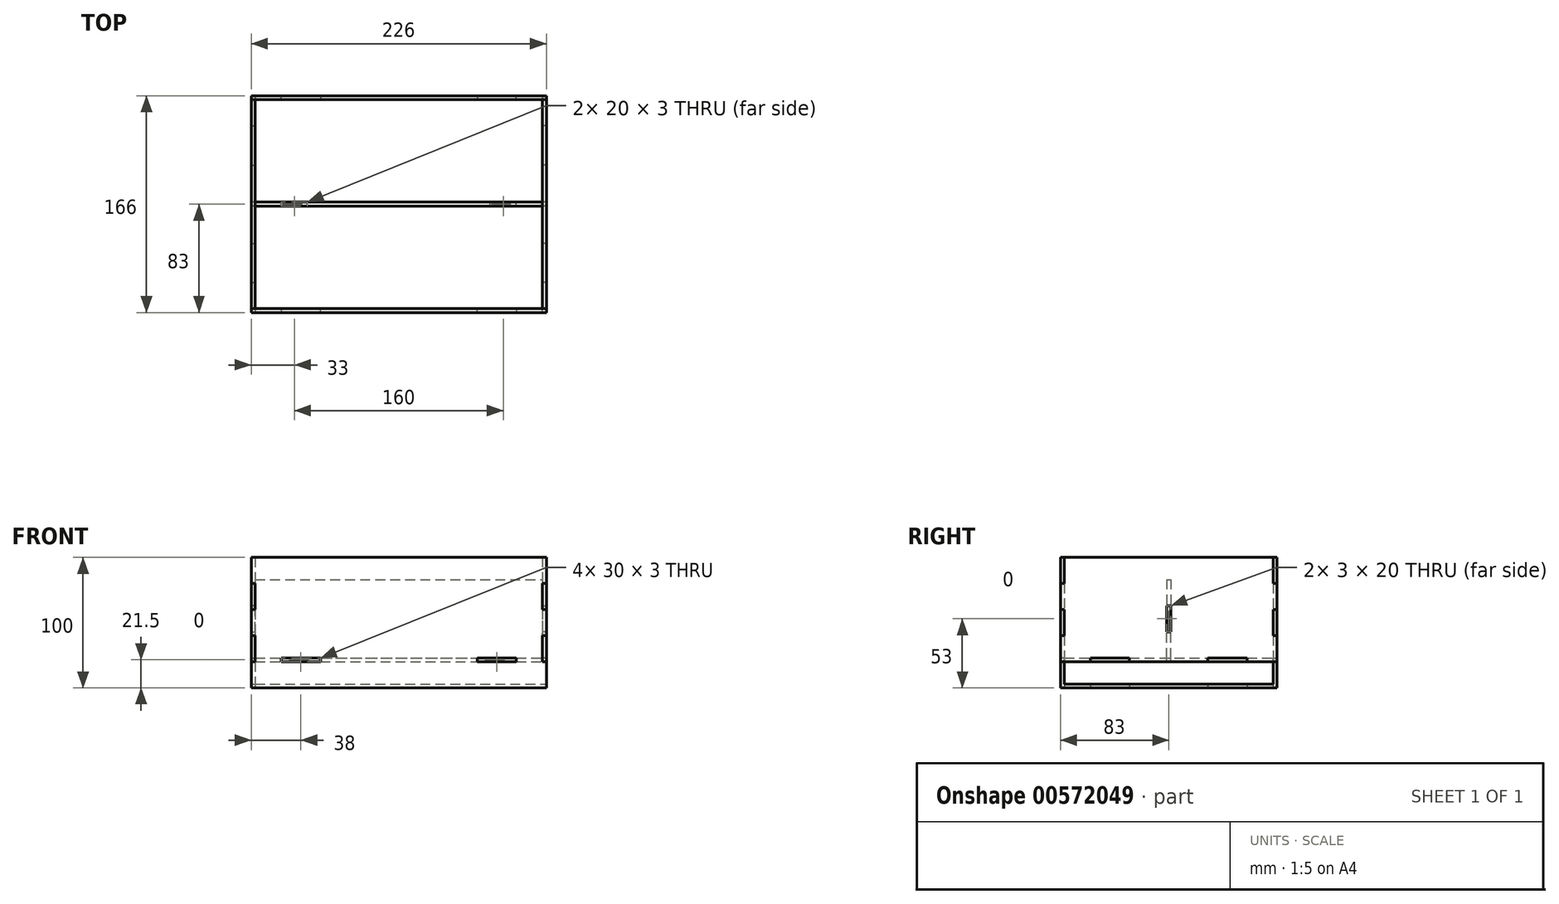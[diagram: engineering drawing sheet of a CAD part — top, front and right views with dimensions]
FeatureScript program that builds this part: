
annotation { "Feature Type Name" : "Feature", "Feature Type Description" : "" }
export const myFeature = defineFeature(function(context is Context, id is Id, definition is map)
    precondition{}
    {
        {
            var Q0;
            Q0=qCreatedBy(makeId("Top.planeOp"),FACE);
            var sketch = newSketch(context, id + "F0", { "sketchPlane" : qUnion([Q0])});
            skLineSegment(sketch, "E0.bottom", {"start": v(-110, -80) * mm, "end": v(-90, -80) * mm});
            skLineSegment(sketch, "E0.top", {"start": v(-110, 80) * mm, "end": v(-90, 80) * mm});
            skLineSegment(sketch, "E0.left", {"start": v(-110, -80) * mm, "end": v(-110, -60) * mm});
            skLineSegment(sketch, "E0.right", {"start": v(110, -80) * mm, "end": v(110, -60) * mm});
            skPoint(sketch, "E0.middle", {"position": v(0, 0) * mm});
            skLineSegment(sketch, "E1", {"start": v(-90, 80) * mm, "end": v(-90, 83) * mm});
            skLineSegment(sketch, "E2", {"start": v(-90, 83) * mm, "end": v(-60, 83) * mm});
            skLineSegment(sketch, "E3", {"start": v(-60, 83) * mm, "end": v(-60, 80) * mm});
            skLineSegment(sketch, "E4.trimOffspring", {"start": v(-60, 80) * mm, "end": v(60, 80) * mm});
            skLineSegment(sketch, "E5.MirrorCS", {"start": v(90, 80) * mm, "end": v(90, 83) * mm});
            skLineSegment(sketch, "E6.MirrorCS", {"start": v(60, 83) * mm, "end": v(60, 80) * mm});
            skLineSegment(sketch, "E7.MirrorCS", {"start": v(90, 83) * mm, "end": v(60, 83) * mm});
            skLineSegment(sketch, "E8.MirrorCS", {"start": v(-90, -80) * mm, "end": v(-90, -83) * mm});
            skLineSegment(sketch, "E9.MirrorCS", {"start": v(-90, -83) * mm, "end": v(-60, -83) * mm});
            skLineSegment(sketch, "E10.MirrorCS", {"start": v(-60, -83) * mm, "end": v(-60, -80) * mm});
            skLineSegment(sketch, "E11.MirrorCS", {"start": v(60, -83) * mm, "end": v(60, -80) * mm});
            skLineSegment(sketch, "E12.MirrorCS", {"start": v(90, -83) * mm, "end": v(60, -83) * mm});
            skLineSegment(sketch, "E13.MirrorCS", {"start": v(90, -80) * mm, "end": v(90, -83) * mm});
            skLineSegment(sketch, "E14.trimOffspring", {"start": v(-60, -80) * mm, "end": v(60, -80) * mm});
            skLineSegment(sketch, "E15.trimOffspring", {"start": v(90, -80) * mm, "end": v(110, -80) * mm});
            skLineSegment(sketch, "E16.trimOffspring", {"start": v(90, 80) * mm, "end": v(110, 80) * mm});
            skLineSegment(sketch, "E17", {"start": v(-113, 60) * mm, "end": v(-110, 60) * mm});
            skLineSegment(sketch, "E18.MirrorCS", {"start": v(-110, 30) * mm, "end": v(-113, 30) * mm});
            skLineSegment(sketch, "E19.MirrorCS", {"start": v(-113, 30) * mm, "end": v(-113, 60) * mm});
            skLineSegment(sketch, "E20.trimOffspring", {"start": v(-110, 60) * mm, "end": v(-110, 80) * mm});
            skLineSegment(sketch, "E21.MirrorCS", {"start": v(-110, -30) * mm, "end": v(-113, -30) * mm});
            skLineSegment(sketch, "E22.MirrorCS", {"start": v(-113, -60) * mm, "end": v(-110, -60) * mm});
            skLineSegment(sketch, "E23.MirrorCS", {"start": v(-113, -30) * mm, "end": v(-113, -60) * mm});
            skLineSegment(sketch, "E24.MirrorCS", {"start": v(113, 60) * mm, "end": v(110, 60) * mm});
            skLineSegment(sketch, "E25.MirrorCS", {"start": v(113, 30) * mm, "end": v(113, 60) * mm});
            skLineSegment(sketch, "E26.MirrorCS", {"start": v(110, 30) * mm, "end": v(113, 30) * mm});
            skLineSegment(sketch, "E27.MirrorCS", {"start": v(110, -30) * mm, "end": v(113, -30) * mm});
            skLineSegment(sketch, "E28.MirrorCS", {"start": v(113, -60) * mm, "end": v(110, -60) * mm});
            skLineSegment(sketch, "E29.MirrorCS", {"start": v(113, -30) * mm, "end": v(113, -60) * mm});
            skLineSegment(sketch, "E30.trimOffspring", {"start": v(110, 60) * mm, "end": v(110, 80) * mm});
            skLineSegment(sketch, "E31.trimOffspring", {"start": v(110, -30) * mm, "end": v(110, 30) * mm});
            skLineSegment(sketch, "E32.trimOffspring", {"start": v(-110, -30) * mm, "end": v(-110, 30) * mm});
            skSolve(sketch);
        }
        {
            var Q0;
            Q0 = qSketchRegion(id + "F0", true);
            extrude(context, id + "F1", {"entities" : qUnion([Q0]), "endBound" : BoundingType.SYMMETRIC, "depth" : 3 * mm, "offsetDistance" : 25 * mm});
        }
        {
            var Q0;
            Q0=makeQuery(id+"F1.opExtrude","SWEPT_FACE",FACE,{"disambiguationData":[OSD([sQuery(id+"F0.wireOp",EDGE,"E32.trimOffspring")])]});
            var sketch = newSketch(context, id + "F2", { "sketchPlane" : qUnion([Q0])});
            skLineSegment(sketch, "E33", {"start": v(-30, 1.5) * mm, "end": v(-60, 1.5) * mm});
            skLineSegment(sketch, "E34", {"start": v(60, 1.5) * mm, "end": v(30, 1.5) * mm});
            skLineSegment(sketch, "E35", {"start": v(-60, -1.5) * mm, "end": v(-80, -1.5) * mm});
            skLineSegment(sketch, "E36", {"start": v(-60, 1.5) * mm, "end": v(-60, -1.5) * mm});
            skLineSegment(sketch, "E37", {"start": v(30, -1.5) * mm, "end": v(-30, -1.5) * mm});
            skLineSegment(sketch, "E38", {"start": v(30, 1.5) * mm, "end": v(30, -1.5) * mm});
            skLineSegment(sketch, "E39", {"start": v(-30, 1.5) * mm, "end": v(-30, -1.5) * mm});
            skLineSegment(sketch, "E40", {"start": v(80, -1.5) * mm, "end": v(60, -1.5) * mm});
            skLineSegment(sketch, "E41", {"start": v(60, 1.5) * mm, "end": v(60, -1.5) * mm});
            skPoint(sketch, "E42.end.orphan", {"position": v(-30, 1.5) * mm});
            skPoint(sketch, "E42.start.orphan", {"position": v(30, 1.5) * mm});
            skPoint(sketch, "E43.end.orphan", {"position": v(60, 1.5) * mm});
            skPoint(sketch, "E44.start.orphan", {"position": v(-60, 1.5) * mm});
            skLineSegment(sketch, "E45", {"start": v(-80, 58.5) * mm, "end": v(-80, 38.5) * mm});
            skLineSegment(sketch, "E46", {"start": v(-80, 38.5) * mm, "end": v(-83, 38.5) * mm});
            skLineSegment(sketch, "E47", {"start": v(-83, 38.5) * mm, "end": v(-83, 18.5) * mm});
            skLineSegment(sketch, "E48", {"start": v(-83, 18.5) * mm, "end": v(-80, 18.5) * mm});
            skLineSegment(sketch, "E49.trimOffspring", {"start": v(-80, 18.5) * mm, "end": v(-80, -1.5) * mm});
            skLineSegment(sketch, "E50.MirrorCS", {"start": v(83, 18.5) * mm, "end": v(80, 18.5) * mm});
            skLineSegment(sketch, "E51.MirrorCS", {"start": v(80, 38.5) * mm, "end": v(83, 38.5) * mm});
            skLineSegment(sketch, "E52.MirrorCS", {"start": v(83, 38.5) * mm, "end": v(83, 18.5) * mm});
            skLineSegment(sketch, "E53.MirrorCS", {"start": v(80, 18.5) * mm, "end": v(80, -1.5) * mm});
            skLineSegment(sketch, "E54.MirrorCS", {"start": v(80, 58.5) * mm, "end": v(80, 38.5) * mm});
            skLineSegment(sketch, "E55", {"start": v(-80, 98.5) * mm, "end": v(-80, 78.5) * mm});
            skLineSegment(sketch, "E56", {"start": v(-80, 78.5) * mm, "end": v(-83, 78.5) * mm});
            skLineSegment(sketch, "E57", {"start": v(-83, 78.5) * mm, "end": v(-83, 58.5) * mm});
            skLineSegment(sketch, "E58", {"start": v(-83, 58.5) * mm, "end": v(-80, 58.5) * mm});
            skLineSegment(sketch, "E59.MirrorCS", {"start": v(80, 98.5) * mm, "end": v(80, 78.5) * mm});
            skLineSegment(sketch, "E60.MirrorCS", {"start": v(80, 78.5) * mm, "end": v(83, 78.5) * mm});
            skLineSegment(sketch, "E61.MirrorCS", {"start": v(83, 58.5) * mm, "end": v(80, 58.5) * mm});
            skLineSegment(sketch, "E62.MirrorCS", {"start": v(83, 78.5) * mm, "end": v(83, 58.5) * mm});
            skLineSegment(sketch, "E63", {"start": v(-80, 98.5) * mm, "end": v(80, 98.5) * mm});
            skSolve(sketch);
        }
        {
            var Q0;
            Q0 = qSketchRegion(id + "F2", true);
            extrude(context, id + "F3", {"entities" : qUnion([Q0]), "depth" : 3 * mm, "offsetDistance" : 25 * mm});
        }
        {
            var Q0;
            Q0=makeQuery(id+"F1.opExtrude","SWEPT_FACE",FACE,{"disambiguationData":[OSD([sQuery(id+"F0.wireOp",EDGE,"E4.trimOffspring")])]});
            var sketch = newSketch(context, id + "F4", { "sketchPlane" : qUnion([Q0])});
            skLineSegment(sketch, "E64", {"start": v(60, -1.5) * mm, "end": v(-60, -1.5) * mm});
            skLineSegment(sketch, "E65.0.1", {"start": v(-90, -1.5) * mm, "end": v(-90, 1.5) * mm});
            skLineSegment(sketch, "E66.0.0", {"start": v(-60, -1.5) * mm, "end": v(60, -1.5) * mm});
            skLineSegment(sketch, "E66.0.1", {"start": v(60, -1.5) * mm, "end": v(60, 1.5) * mm});
            skLineSegment(sketch, "E66.0.3", {"start": v(-60, 1.5) * mm, "end": v(-60, -1.5) * mm});
            skLineSegment(sketch, "E67.0.3", {"start": v(90, 1.5) * mm, "end": v(90, -1.5) * mm});
            skLineSegment(sketch, "E68.0.1", {"start": v(90, -1.5) * mm, "end": v(90, 1.5) * mm});
            skLineSegment(sketch, "E68.0.2", {"start": v(90, 1.5) * mm, "end": v(60, 1.5) * mm});
            skLineSegment(sketch, "E68.0.3", {"start": v(60, 1.5) * mm, "end": v(60, -1.5) * mm});
            skLineSegment(sketch, "E69.0.1", {"start": v(-60, -1.5) * mm, "end": v(-60, 1.5) * mm});
            skLineSegment(sketch, "E69.0.2", {"start": v(-60, 1.5) * mm, "end": v(-90, 1.5) * mm});
            skLineSegment(sketch, "E69.0.3", {"start": v(-90, 1.5) * mm, "end": v(-90, -1.5) * mm});
            skPoint(sketch, "E70.end.orphan", {"position": v(-90, -1.5) * mm});
            skPoint(sketch, "E70.start.orphan", {"position": v(-60, -1.5) * mm});
            skPoint(sketch, "E71.end.orphan", {"position": v(60, -1.5) * mm});
            skPoint(sketch, "E71.start.orphan", {"position": v(90, -1.5) * mm});
            skLineSegment(sketch, "E72", {"start": v(90, -1.5) * mm, "end": v(113, -1.5) * mm});
            skLineSegment(sketch, "E73", {"start": v(-90, -1.5) * mm, "end": v(-113, -1.5) * mm});
            skLineSegment(sketch, "E74", {"start": v(-113, 38.5) * mm, "end": v(-110, 38.5) * mm});
            skLineSegment(sketch, "E75", {"start": v(-110, 38.5) * mm, "end": v(-110, 18.5) * mm});
            skLineSegment(sketch, "E76", {"start": v(-110, 18.5) * mm, "end": v(-113, 18.5) * mm});
            skLineSegment(sketch, "E77.trimOffspring", {"start": v(-113, 18.5) * mm, "end": v(-113, -1.5) * mm});
            skLineSegment(sketch, "E78.MirrorCS", {"start": v(113, 38.5) * mm, "end": v(110, 38.5) * mm});
            skLineSegment(sketch, "E79.MirrorCS", {"start": v(110, 18.5) * mm, "end": v(113, 18.5) * mm});
            skLineSegment(sketch, "E80.MirrorCS", {"start": v(113, 58.5) * mm, "end": v(113, 38.5) * mm});
            skLineSegment(sketch, "E81.MirrorCS", {"start": v(110, 38.5) * mm, "end": v(110, 18.5) * mm});
            skLineSegment(sketch, "E82.MirrorCS", {"start": v(113, 18.5) * mm, "end": v(113, -1.5) * mm});
            skPoint(sketch, "E83.visualSharp", {"position": v(-113, 58.5) * mm});
            skLineSegment(sketch, "E84", {"start": v(-113, 38.5) * mm, "end": v(-113, 58.5) * mm});
            skLineSegment(sketch, "E85", {"start": v(-113, 58.5) * mm, "end": v(-110, 58.5) * mm});
            skLineSegment(sketch, "E86", {"start": v(-113, 78.5) * mm, "end": v(-110, 78.5) * mm});
            skLineSegment(sketch, "E87", {"start": v(-110, 78.5) * mm, "end": v(-110, 58.5) * mm});
            skLineSegment(sketch, "E88", {"start": v(-110, 58.5) * mm, "end": v(-113, 58.5) * mm});
            skLineSegment(sketch, "E89", {"start": v(-113, 78.5) * mm, "end": v(-113, 98.5) * mm});
            skLineSegment(sketch, "E90.MirrorCS", {"start": v(113, 58.5) * mm, "end": v(110, 58.5) * mm});
            skLineSegment(sketch, "E91.MirrorCS", {"start": v(110, 78.5) * mm, "end": v(110, 58.5) * mm});
            skLineSegment(sketch, "E92.MirrorCS", {"start": v(113, 78.5) * mm, "end": v(113, 98.5) * mm});
            skLineSegment(sketch, "E93.MirrorCS", {"start": v(113, 78.5) * mm, "end": v(110, 78.5) * mm});
            skLineSegment(sketch, "E94", {"start": v(-113, 98.5) * mm, "end": v(113, 98.5) * mm});
            skLineSegment(sketch, "E95.0.1", {"start": v(-60, 18.5) * mm, "end": v(-60, 21.5) * mm});
            skLineSegment(sketch, "E95.0.2", {"start": v(-60, 21.5) * mm, "end": v(-90, 21.5) * mm});
            skLineSegment(sketch, "E95.0.3", {"start": v(-90, 21.5) * mm, "end": v(-90, 18.5) * mm});
            skLineSegment(sketch, "E96", {"start": v(-90, 18.5) * mm, "end": v(-60, 18.5) * mm});
            skLineSegment(sketch, "E97.MirrorCS", {"start": v(90, 21.5) * mm, "end": v(90, 18.5) * mm});
            skLineSegment(sketch, "E98.MirrorCS", {"start": v(60, 18.5) * mm, "end": v(60, 21.5) * mm});
            skLineSegment(sketch, "E99.MirrorCS", {"start": v(60, 21.5) * mm, "end": v(90, 21.5) * mm});
            skLineSegment(sketch, "E100.MirrorCS", {"start": v(90, 18.5) * mm, "end": v(60, 18.5) * mm});
            skSolve(sketch);
        }
        {
            var Q0;
            Q0 = qSketchRegion(id + "F4", true);
            extrude(context, id + "F5", {"entities" : qUnion([Q0]), "depth" : 3 * mm, "offsetDistance" : 25 * mm});
        }
        {
            var Q0;
            Q0=makeQuery(id+"F5.opExtrude","SWEPT_BODY",BODY,{"disambiguationData":[OSD([sQuery(id+"F4.wireOp",EDGE,"rkJhuVlj-TpCy-ekKi-Wodk-7rqdhOQi29P6"),sQuery(id+"F4.wireOp",EDGE,"E66.0.0"),sQuery(id+"F4.wireOp",EDGE,"E68.0.1"),sQuery(id+"F4.wireOp",EDGE,"E68.0.2"),sQuery(id+"F4.wireOp",EDGE,"E68.0.3"),sQuery(id+"F4.wireOp",EDGE,"E69.0.1"),sQuery(id+"F4.wireOp",EDGE,"E69.0.2"),sQuery(id+"F4.wireOp",EDGE,"E69.0.3"),sQuery(id+"F4.wireOp",EDGE,"E72"),sQuery(id+"F4.wireOp",EDGE,"K4oBUEiu-vONG-t3VU-zjAf-cytJRjsT2u9M"),sQuery(id+"F4.wireOp",EDGE,"E73"),sQuery(id+"F4.wireOp",EDGE,"E74"),sQuery(id+"F4.wireOp",EDGE,"E75"),sQuery(id+"F4.wireOp",EDGE,"E76"),sQuery(id+"F4.wireOp",EDGE,"E77.trimOffspring"),sQuery(id+"F4.wireOp",EDGE,"E78.MirrorCS"),sQuery(id+"F4.wireOp",EDGE,"E79.MirrorCS"),sQuery(id+"F4.wireOp",EDGE,"E80.MirrorCS"),sQuery(id+"F4.wireOp",EDGE,"E81.MirrorCS"),sQuery(id+"F4.wireOp",EDGE,"E82.MirrorCS")])]});
            var Q1;
            Q1=qCreatedBy(makeId("Front.planeOp"),FACE);
            mirror(context, id + "F6", {"entities" : qUnion([Q0]), "mirrorPlane" : qUnion([Q1])});
        }
        {
            var Q0;
            Q0=qCreatedBy(makeId("Top.planeOp"),FACE);
            cPlane(context, id + "F7", {"entities" : qUnion([Q0]), "cplaneType" : CPlaneType.OFFSET, "offset" : 10 * mm, "width" : 150 * mm, "height" : 150 * mm});
        }
        {
            var Q0;
            Q0=makeQuery(id+"F1.opExtrude","SWEPT_BODY",BODY,{"disambiguationData":[OSD([sQuery(id+"F0.wireOp",EDGE,"E0.bottom"),sQuery(id+"F0.wireOp",EDGE,"E0.top"),sQuery(id+"F0.wireOp",EDGE,"E0.left"),sQuery(id+"F0.wireOp",EDGE,"E0.right"),sQuery(id+"F0.wireOp",EDGE,"E4.trimOffspring"),sQuery(id+"F0.wireOp",EDGE,"E5.MirrorCS"),sQuery(id+"F0.wireOp",EDGE,"E6.MirrorCS"),sQuery(id+"F0.wireOp",EDGE,"E7.MirrorCS"),sQuery(id+"F0.wireOp",EDGE,"E1"),sQuery(id+"F0.wireOp",EDGE,"E2"),sQuery(id+"F0.wireOp",EDGE,"E3"),sQuery(id+"F0.wireOp",EDGE,"E8.MirrorCS"),sQuery(id+"F0.wireOp",EDGE,"E9.MirrorCS"),sQuery(id+"F0.wireOp",EDGE,"E10.MirrorCS"),sQuery(id+"F0.wireOp",EDGE,"E11.MirrorCS"),sQuery(id+"F0.wireOp",EDGE,"E12.MirrorCS"),sQuery(id+"F0.wireOp",EDGE,"E13.MirrorCS"),sQuery(id+"F0.wireOp",EDGE,"E14.trimOffspring"),sQuery(id+"F0.wireOp",EDGE,"E15.trimOffspring"),sQuery(id+"F0.wireOp",EDGE,"E16.trimOffspring"),sQuery(id+"F0.wireOp",EDGE,"E17"),sQuery(id+"F0.wireOp",EDGE,"E18.MirrorCS"),sQuery(id+"F0.wireOp",EDGE,"E19.MirrorCS"),sQuery(id+"F0.wireOp",EDGE,"E20.trimOffspring"),sQuery(id+"F0.wireOp",EDGE,"E21.MirrorCS"),sQuery(id+"F0.wireOp",EDGE,"E22.MirrorCS"),sQuery(id+"F0.wireOp",EDGE,"E23.MirrorCS"),sQuery(id+"F0.wireOp",EDGE,"E24.MirrorCS"),sQuery(id+"F0.wireOp",EDGE,"E25.MirrorCS"),sQuery(id+"F0.wireOp",EDGE,"E26.MirrorCS"),sQuery(id+"F0.wireOp",EDGE,"E27.MirrorCS"),sQuery(id+"F0.wireOp",EDGE,"E28.MirrorCS"),sQuery(id+"F0.wireOp",EDGE,"E29.MirrorCS"),sQuery(id+"F0.wireOp",EDGE,"E30.trimOffspring"),sQuery(id+"F0.wireOp",EDGE,"E31.trimOffspring"),sQuery(id+"F0.wireOp",EDGE,"E32.trimOffspring")])]});
            var Q1;
            Q1=qCreatedBy(id+"F7.planeOp",FACE);
            mirror(context, id + "F8", {"entities" : qUnion([Q0]), "mirrorPlane" : qUnion([Q1])});
        }
        {
            var Q0;
            Q0=makeQuery(id+"F8.opPattern","COPY",FACE,{"derivedFrom":makeQuery(id+"F1.opExtrude","SWEPT_FACE",FACE,{"disambiguationData":[OSD([sQuery(id+"F0.wireOp",EDGE,"E31.trimOffspring")])]}),"instanceName":"1"});
            var sketch = newSketch(context, id + "F9", { "sketchPlane" : qUnion([Q0])});
            skLineSegment(sketch, "E101.bottom", {"start": v(-80, 98.5) * mm, "end": v(80, 98.5) * mm});
            skLineSegment(sketch, "E101.left", {"start": v(-80, 98.5) * mm, "end": v(-80, 78.5) * mm});
            skLineSegment(sketch, "E102", {"start": v(-83, 78.5) * mm, "end": v(-80, 78.5) * mm});
            skLineSegment(sketch, "E103", {"start": v(-83, 78.5) * mm, "end": v(-83, 58.5) * mm});
            skLineSegment(sketch, "E104", {"start": v(-83, 58.5) * mm, "end": v(-80, 58.5) * mm});
            skLineSegment(sketch, "E105", {"start": v(-83, 38.5) * mm, "end": v(-80, 38.5) * mm});
            skLineSegment(sketch, "E106", {"start": v(-83, 38.5) * mm, "end": v(-83, 18.5) * mm});
            skLineSegment(sketch, "E107.trimOffspring", {"start": v(-80, 58.5) * mm, "end": v(-80, 38.5) * mm});
            skLineSegment(sketch, "E108.MirrorCS", {"start": v(83, 38.5) * mm, "end": v(83, 18.5) * mm});
            skLineSegment(sketch, "E109.MirrorCS", {"start": v(83, 38.5) * mm, "end": v(80, 38.5) * mm});
            skLineSegment(sketch, "E110.MirrorCS", {"start": v(80, 58.5) * mm, "end": v(80, 38.5) * mm});
            skLineSegment(sketch, "E111.MirrorCS", {"start": v(83, 58.5) * mm, "end": v(80, 58.5) * mm});
            skLineSegment(sketch, "E112.MirrorCS", {"start": v(83, 78.5) * mm, "end": v(83, 58.5) * mm});
            skLineSegment(sketch, "E113.MirrorCS", {"start": v(80, 98.5) * mm, "end": v(80, 78.5) * mm});
            skLineSegment(sketch, "E114.MirrorCS", {"start": v(83, 78.5) * mm, "end": v(80, 78.5) * mm});
            skLineSegment(sketch, "E115", {"start": v(-30, 18.5) * mm, "end": v(-30, 21.5) * mm});
            skLineSegment(sketch, "E116.bottom", {"start": v(-60, 21.5) * mm, "end": v(-30, 21.5) * mm});
            skLineSegment(sketch, "E116.left", {"start": v(-60, 21.5) * mm, "end": v(-60, 18.5) * mm});
            skLineSegment(sketch, "E117.bottom", {"start": v(30, 21.5) * mm, "end": v(60, 21.5) * mm});
            skLineSegment(sketch, "E117.left", {"start": v(30, 21.5) * mm, "end": v(30, 18.5) * mm});
            skLineSegment(sketch, "E117.right", {"start": v(60, 21.5) * mm, "end": v(60, 18.5) * mm});
            skPoint(sketch, "E101.top.start.orphan", {"position": v(-80, -1.5) * mm});
            skPoint(sketch, "E118.MirrorCS.end.orphan", {"position": v(80, -1.5) * mm});
            skPoint(sketch, "E119.MirrorCS.end.orphan", {"position": v(80, 18.5) * mm});
            skPoint(sketch, "E119.MirrorCS.start.orphan", {"position": v(83, 18.5) * mm});
            skPoint(sketch, "E120.end.orphan", {"position": v(-80, 18.5) * mm});
            skPoint(sketch, "E120.start.orphan", {"position": v(-83, 18.5) * mm});
            skLineSegment(sketch, "E121", {"start": v(-83, 18.5) * mm, "end": v(-60, 18.5) * mm});
            skLineSegment(sketch, "E122", {"start": v(60, 18.5) * mm, "end": v(83, 18.5) * mm});
            skLineSegment(sketch, "E123", {"start": v(-30, 18.5) * mm, "end": v(30, 18.5) * mm});
            skSolve(sketch);
        }
        {
            var Q0;
            Q0 = qSketchRegion(id + "F9", true);
            extrude(context, id + "F10", {"entities" : qUnion([Q0]), "depth" : 3 * mm, "offsetDistance" : 25 * mm});
        }
        {
            var Q0;
            Q0=makeQuery(id+"F1.opExtrude","SWEPT_FACE",FACE,{"disambiguationData":[OSD([sQuery(id+"F0.wireOp",EDGE,"E31.trimOffspring")])]});
            var sketch = newSketch(context, id + "F11", { "sketchPlane" : qUnion([Q0])});
            skLineSegment(sketch, "E124.bottom", {"start": v(-30, 1.5) * mm, "end": v(30, 1.5) * mm});
            skLineSegment(sketch, "E124.top", {"start": v(-30, -1.5) * mm, "end": v(30, -1.5) * mm});
            skLineSegment(sketch, "E124.left", {"start": v(-30, 1.5) * mm, "end": v(-30, -1.5) * mm});
            skLineSegment(sketch, "E124.right", {"start": v(30, 1.5) * mm, "end": v(30, -1.5) * mm});
            skLineSegment(sketch, "E125.bottom", {"start": v(-80, 1.5) * mm, "end": v(-60, 1.5) * mm});
            skLineSegment(sketch, "E125.top", {"start": v(-80, -1.5) * mm, "end": v(-60, -1.5) * mm});
            skLineSegment(sketch, "E125.left", {"start": v(-80, 1.5) * mm, "end": v(-80, -1.5) * mm});
            skLineSegment(sketch, "E125.right", {"start": v(-60, 1.5) * mm, "end": v(-60, -1.5) * mm});
            skLineSegment(sketch, "E126.bottom", {"start": v(60, 1.5) * mm, "end": v(80, 1.5) * mm});
            skLineSegment(sketch, "E126.top", {"start": v(60, -1.5) * mm, "end": v(80, -1.5) * mm});
            skLineSegment(sketch, "E126.left", {"start": v(60, 1.5) * mm, "end": v(60, -1.5) * mm});
            skLineSegment(sketch, "E126.right", {"start": v(80, 1.5) * mm, "end": v(80, -1.5) * mm});
            skSolve(sketch);
        }
        {
            var Q0;
            Q0 = qSketchRegion(id + "F11", true);
            extrude(context, id + "F12", {"entities" : qUnion([Q0]), "operationType" : NewBodyOperationType.ADD, "depth" : 3 * mm, "offsetDistance" : 25 * mm});
        }
        {
            var Q0;
            Q0=qCreatedBy(makeId("Front.planeOp"),FACE);
            var sketch = newSketch(context, id + "F13", { "sketchPlane" : qUnion([Q0])});
            skLineSegment(sketch, "E127.bottom", {"start": v(110, 81.5) * mm, "end": v(-110, 81.5) * mm});
            skLineSegment(sketch, "E127.top", {"start": v(110, 21.5) * mm, "end": v(90, 21.5) * mm});
            skLineSegment(sketch, "E127.right", {"start": v(-110, 81.5) * mm, "end": v(-110, 61.5) * mm});
            skLineSegment(sketch, "E128", {"start": v(-110, 61.5) * mm, "end": v(-113, 61.5) * mm});
            skLineSegment(sketch, "E129", {"start": v(-113, 61.5) * mm, "end": v(-113, 41.5) * mm});
            skLineSegment(sketch, "E130", {"start": v(-113, 41.5) * mm, "end": v(-110, 41.5) * mm});
            skLineSegment(sketch, "E131.trimOffspring", {"start": v(-110, 41.5) * mm, "end": v(-110, 21.5) * mm});
            skLineSegment(sketch, "E132.MirrorCS", {"start": v(110, 61.5) * mm, "end": v(113, 61.5) * mm});
            skLineSegment(sketch, "E133.MirrorCS", {"start": v(113, 41.5) * mm, "end": v(110, 41.5) * mm});
            skLineSegment(sketch, "E134.MirrorCS", {"start": v(-110, 21.5) * mm, "end": v(-90, 21.5) * mm});
            skLineSegment(sketch, "E135.MirrorCS", {"start": v(110, 41.5) * mm, "end": v(110, 21.5) * mm});
            skLineSegment(sketch, "E136.MirrorCS", {"start": v(113, 61.5) * mm, "end": v(113, 41.5) * mm});
            skLineSegment(sketch, "E137.MirrorCS", {"start": v(110, 81.5) * mm, "end": v(110, 61.5) * mm});
            skLineSegment(sketch, "E138.MirrorCS", {"start": v(90, 21.5) * mm, "end": v(90, 18.5) * mm});
            skLineSegment(sketch, "E139.MirrorCS", {"start": v(70, 18.5) * mm, "end": v(70, 21.5) * mm});
            skLineSegment(sketch, "E140.MirrorCS", {"start": v(90, 18.5) * mm, "end": v(70, 18.5) * mm});
            skLineSegment(sketch, "E141.MirrorCS", {"start": v(-70, 18.5) * mm, "end": v(-70, 21.5) * mm});
            skLineSegment(sketch, "E142.MirrorCS", {"start": v(-90, 21.5) * mm, "end": v(-90, 18.5) * mm});
            skLineSegment(sketch, "E143.MirrorCS", {"start": v(-90, 18.5) * mm, "end": v(-70, 18.5) * mm});
            skLineSegment(sketch, "E144.trimOffspring", {"start": v(70, 21.5) * mm, "end": v(-70, 21.5) * mm});
            skLineSegment(sketch, "E145.trimOffspring", {"start": v(-90, 21.5) * mm, "end": v(-110, 21.5) * mm});
            skLineSegment(sketch, "E146.trimOffspring", {"start": v(-70, 21.5) * mm, "end": v(70, 21.5) * mm});
            skLineSegment(sketch, "E147.trimOffspring", {"start": v(90, 21.5) * mm, "end": v(110, 21.5) * mm});
            skSolve(sketch);
        }
        {
            var Q0;
            Q0 = qSketchRegion(id + "F13", true);
            extrude(context, id + "F14", {"entities" : qUnion([Q0]), "operationType" : NewBodyOperationType.REMOVE, "endBound" : BoundingType.SYMMETRIC, "depth" : 3 * mm, "offsetDistance" : 25 * mm});
        }
        {
            var Q0;
            Q0=qCreatedBy(makeId("Front.planeOp"),FACE);
            var sketch = newSketch(context, id + "F15", { "sketchPlane" : qUnion([Q0])});
            skLineSegment(sketch, "E148.bottom", {"start": v(-110, 81.5) * mm, "end": v(110, 81.5) * mm});
            skLineSegment(sketch, "E148.top", {"start": v(-110, 21.5) * mm, "end": v(-90, 21.5) * mm});
            skLineSegment(sketch, "E148.left", {"start": v(-110, 81.5) * mm, "end": v(-110, 61.5) * mm});
            skLineSegment(sketch, "E148.right", {"start": v(110, 81.5) * mm, "end": v(110, 61.5) * mm});
            skLineSegment(sketch, "E149", {"start": v(-70, 21.5) * mm, "end": v(70, 21.5) * mm});
            skLineSegment(sketch, "E150", {"start": v(90, 21.5) * mm, "end": v(110, 21.5) * mm});
            skLineSegment(sketch, "E151", {"start": v(110, 61.5) * mm, "end": v(110, 81.5) * mm});
            skLineSegment(sketch, "E152", {"start": v(110, 21.5) * mm, "end": v(110, 41.5) * mm});
            skLineSegment(sketch, "E153.trimOffspring", {"start": v(110, 41.5) * mm, "end": v(110, 21.5) * mm});
            skPoint(sketch, "E154.orphan", {"position": v(110, 98.5) * mm});
            skPoint(sketch, "E155.orphan", {"position": v(110, 18.5) * mm});
            skLineSegment(sketch, "E156", {"start": v(-90, 21.5) * mm, "end": v(-90, 18.5) * mm});
            skLineSegment(sketch, "E157", {"start": v(-90, 18.5) * mm, "end": v(-70, 18.5) * mm});
            skLineSegment(sketch, "E158", {"start": v(-70, 18.5) * mm, "end": v(-70, 21.5) * mm});
            skLineSegment(sketch, "E159", {"start": v(70, 21.5) * mm, "end": v(70, 18.5) * mm});
            skLineSegment(sketch, "E160", {"start": v(70, 18.5) * mm, "end": v(90, 18.5) * mm});
            skLineSegment(sketch, "E161", {"start": v(90, 18.5) * mm, "end": v(90, 21.5) * mm});
            skLineSegment(sketch, "E162", {"start": v(110, 61.5) * mm, "end": v(113, 61.5) * mm});
            skLineSegment(sketch, "E163", {"start": v(113, 61.5) * mm, "end": v(113, 41.5) * mm});
            skLineSegment(sketch, "E164", {"start": v(113, 41.5) * mm, "end": v(110, 41.5) * mm});
            skLineSegment(sketch, "E165.MirrorCS", {"start": v(-113, 41.5) * mm, "end": v(-110, 41.5) * mm});
            skLineSegment(sketch, "E166.MirrorCS", {"start": v(-110, 61.5) * mm, "end": v(-113, 61.5) * mm});
            skLineSegment(sketch, "E167.MirrorCS", {"start": v(-113, 61.5) * mm, "end": v(-113, 41.5) * mm});
            skLineSegment(sketch, "E168.trimOffspring", {"start": v(-110, 41.5) * mm, "end": v(-110, 21.5) * mm});
            skSolve(sketch);
        }
        {
            var Q0;
            Q0 = qSketchRegion(id + "F15", true);
            extrude(context, id + "F16", {"entities" : qUnion([Q0]), "endBound" : BoundingType.SYMMETRIC, "depth" : 3 * mm, "offsetDistance" : 25 * mm});
        }
    });
